# Revit family: Lightronics_LightingFixture_WallAndCeiling_DOTT_XL1
name_source: partatom
category: Lighting Fixtures
revit_build: Autodesk Revit 2016 (Build: 20160314_0715(x64)
units: mm (PartAtom-declared; Revit-internal decimal feet)

## family parameters
Cut with Voids When Loaded = No
Host = Face
Light Source = Yes
OmniClass Number = 23.80.70.00
OmniClass Title = Lighting
Part Type = Normal
Room Calculation Point = No
Round Connector Dimension = Use Diameter
Shared = No

## types (1)
- DOTT XL
    Apparent Load = 0 VA
    Assembly Code = D5020200
    AssetType = Fixed
    BIMObjectName = Lightronics_LightingFixture_WallAndCeiling_DOTT_XL
    ClassificationName = Uniclass 2015
    ClassificationValue = Pr_70_70_48_85
    Color = Housing: aluminium coated (DB703) or RAL 9010. Cover: UV-stabilised polycarbonate opal or frosted
    Color Filter = 16777215
    Default Elevation = 1219 mm
    Depth = 500 mm  [stored 1.64042 ft]
    Description = Impact proof surface-mounted design luminaire
    Diameter = 500 mm  [stored 1.64042 ft]
    Dimming Lamp Color Temperature Shift = <None>
    DocumentationLiterature = https://specifi.bimstore.co.uk
    DurationUnit = 20 Years
    Emit Shape Visible in Rendering = No
    Emit from Circle Diameter = 450 mm  [stored 1.47638 ft]
    ExpectedLife = 10
    Height = 115 mm  [stored 0.377297 ft]
    IfcExportAs = IfcLightFixtureTypeEnum.POINTSOURCE
    IfcExportType = IfcLightFixture
    Keynote = V90/510
    Length = 500 mm  [stored 1.64042 ft]
    Manufacturer = Lightronics
    ManufacturerName = Lightronics
    Material = UV-stabilised polycarbonate
    Model = DOTT XL
    ModelNumber = DOTT XL
    ModelReference = IP 65
    NBSDescription = Surface luminaires
    NBSObjectName = Lightronics -  General purpose luminaires
    NBSReference = 90-60-50/405
    NominalDepth = 500 mm  [stored 1.64042 ft]
    NominalHeight = 115 mm  [stored 0.377297 ft]
    NominalLength = 500 mm  [stored 1.64042 ft]
    NumberOfPoles = 1
    Photometric Web File = DOTTXL-LO-1-19-500-D-F-2280-230-X-W.ies
    ProductionYear = 2018
    Shape = Circular
    Size = 500x115
    Tilt Angle = 90.00°
    Type Comments = Wall and ceiling lighting – Hogro Plus. Impact proof surface-mounted design luminaire
    TypeName = DOTT XL
    URL = https://www.lightronics.nl
    Voltage = 230 V
    WarrantyDurationParts = 5
    WarrantyDurationUnit = Years
    _BSBibleVersion = 15
    _BimSpecGuid = 0
    _CurrentRevision = 1
    _DistributedBy = www.bimstore.co.uk

note: [stored X ft] marks values corroborated as IEEE doubles in the binary element streams (Revit-internal decimal feet)

## geometry (parser evidence)
native form markers: Sweep x2
no freeform markers — native parametric forms only
